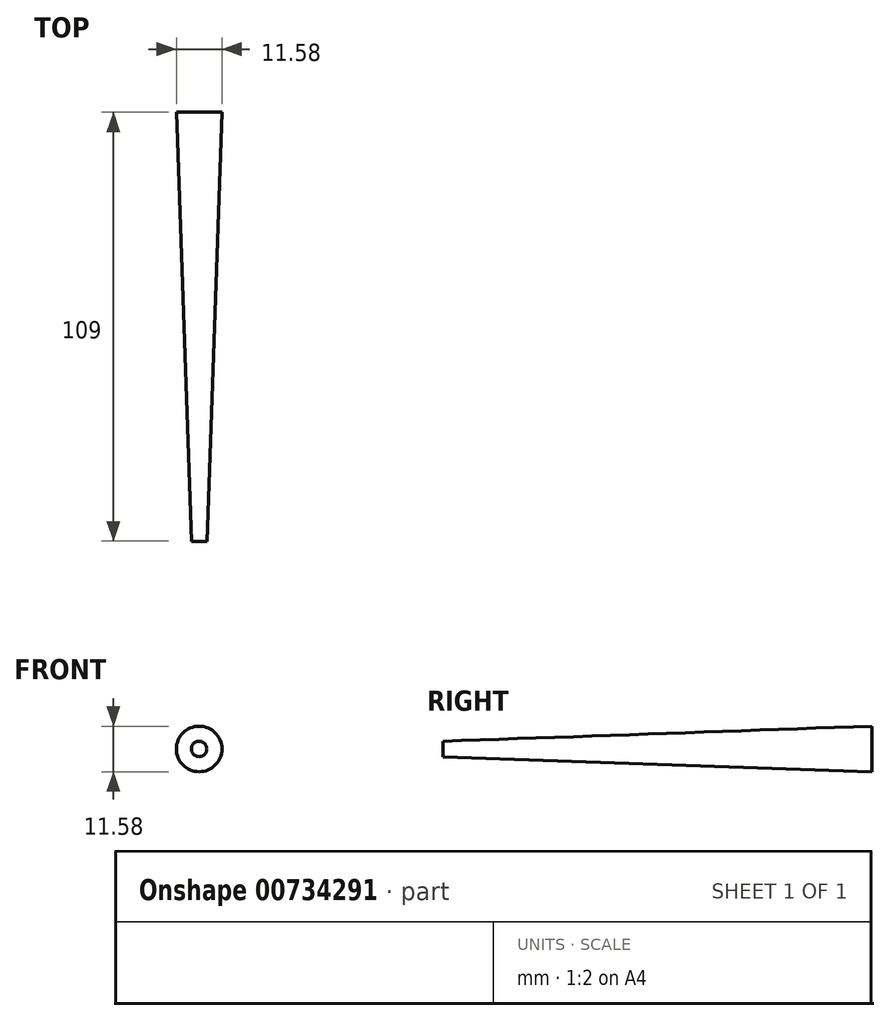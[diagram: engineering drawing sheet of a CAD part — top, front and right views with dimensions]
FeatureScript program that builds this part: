
annotation { "Feature Type Name" : "Feature", "Feature Type Description" : "" }
export const myFeature = defineFeature(function(context is Context, id is Id, definition is map)
    precondition{}
    {
        {
            var Q0;
            Q0=qCreatedBy(makeId("Top.planeOp"),FACE);
            var sketch = newSketch(context, id + "F0", { "sketchPlane" : qUnion([Q0])});
            skLineSegment(sketch, "E0", {"start": v(0, 12.06) * mm, "end": v(-5.8, 12.06) * mm});
            skLineSegment(sketch, "E1", {"start": v(0, -96.94) * mm, "end": v(-1.96, -96.94) * mm});
            skLineSegment(sketch, "E2", {"start": v(-1.96, -96.94) * mm, "end": v(-5.8, 12.06) * mm});
            skLineSegment(sketch, "E3", {"start": v(0, 12.06) * mm, "end": v(0, -96.94) * mm});
            skSolve(sketch);
        }
        {
            var Q0;
            Q0=makeQuery(id+"F0.imprint","IMPRINT",FACE,{"disambiguationData":[TD([[makeQuery(id+"F0.imprint","IMPRINT",EDGE,{"derivedFrom":sQuery(id+"F0.wireOp",EDGE,"E0")}),1.0]])]});
            var Q1;
            Q1=sQuery(id+"F0.wireOp",EDGE,"E3");
            revolve(context, id + "F1", {"surfaceOperationType" : NewSurfaceOperationType.NEW, "entities" : qUnion([Q0]), "axis" : qUnion([Q1]), "revolveType" : RevolveType.FULL});
        }
    });
